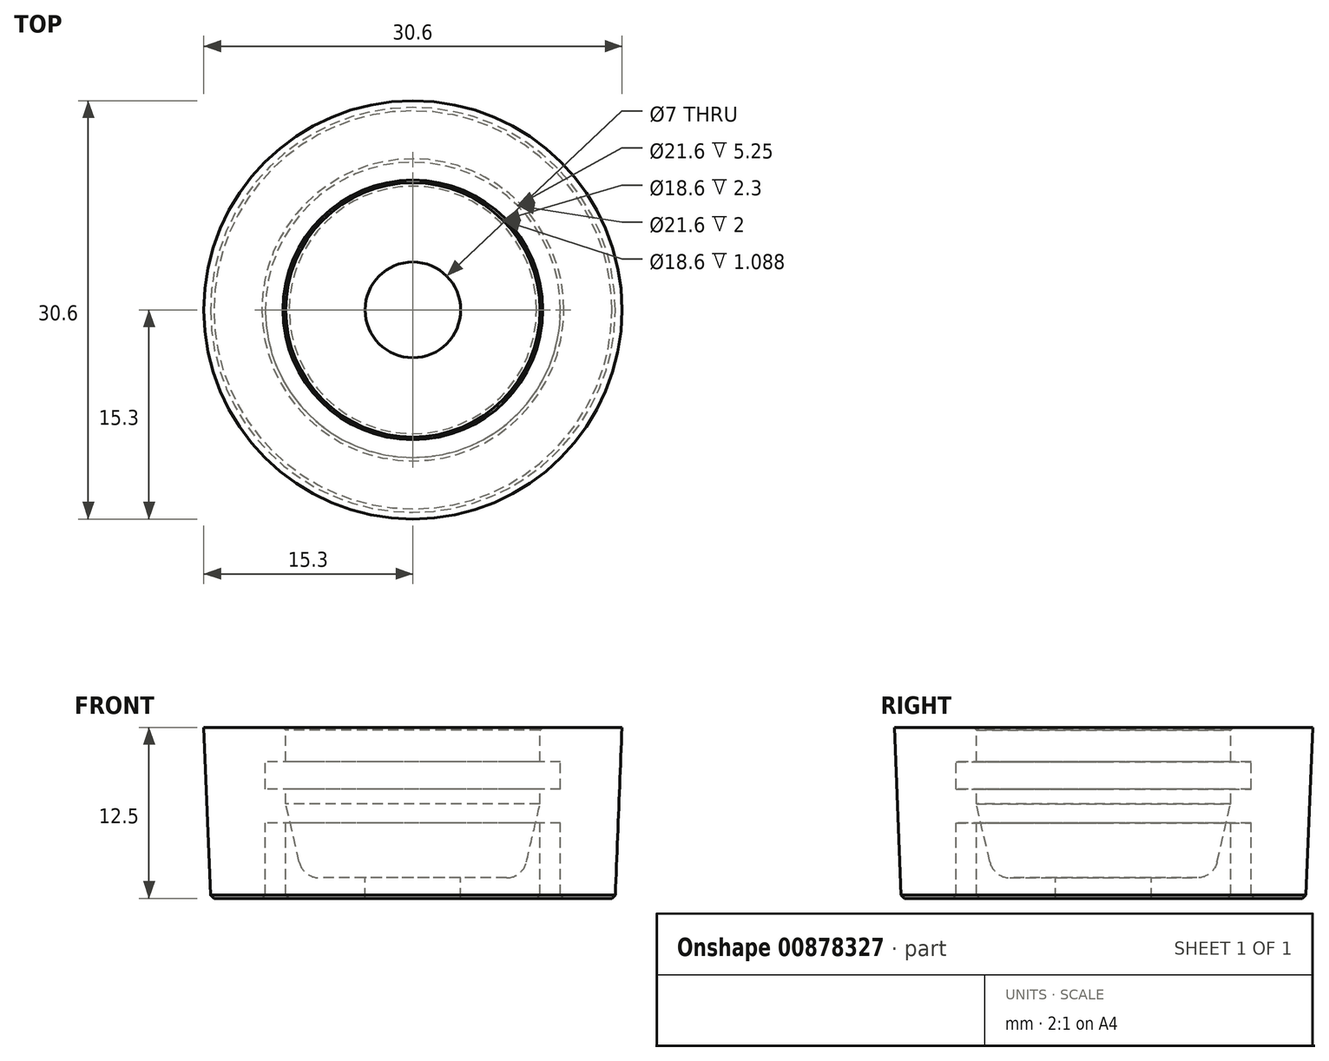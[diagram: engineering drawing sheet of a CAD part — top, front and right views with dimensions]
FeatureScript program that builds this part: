
annotation { "Feature Type Name" : "Feature", "Feature Type Description" : "" }
export const myFeature = defineFeature(function(context is Context, id is Id, definition is map)
    precondition{}
    {
        {
            var Q0;
            Q0=qCreatedBy(makeId("Front.planeOp"),FACE);
            var sketch = newSketch(context, id + "F0", { "sketchPlane" : qUnion([Q0])});
            skLineSegment(sketch, "E0", {"start": v(3.5, -4) * mm, "end": v(8.04, -4) * mm});
            skLineSegment(sketch, "E1", {"start": v(8.04, -4) * mm, "end": v(9.3, 1.41) * mm});
            skLineSegment(sketch, "E2", {"start": v(9.3, 1.41) * mm, "end": v(9.3, 1.41) * mm});
            skLineSegment(sketch, "E3", {"start": v(9.3, 1.41) * mm, "end": v(9.3, 2.5) * mm});
            skLineSegment(sketch, "E4", {"start": v(9.3, 2.5) * mm, "end": v(10.8, 2.5) * mm});
            skLineSegment(sketch, "E5", {"start": v(10.8, 2.5) * mm, "end": v(10.8, 4.5) * mm});
            skLineSegment(sketch, "E6", {"start": v(10.8, 4.5) * mm, "end": v(9.3, 4.5) * mm});
            skLineSegment(sketch, "E7", {"start": v(9.3, 4.5) * mm, "end": v(9.3, 7) * mm});
            skLineSegment(sketch, "E8", {"start": v(9.3, 7) * mm, "end": v(15.3, 7) * mm});
            skLineSegment(sketch, "E9", {"start": v(15.3, 7) * mm, "end": v(14.8, -5.5) * mm});
            skLineSegment(sketch, "E10", {"start": v(14.8, -5.5) * mm, "end": v(10.8, -5.5) * mm});
            skLineSegment(sketch, "E11", {"start": v(10.8, -5.5) * mm, "end": v(10.8, 0) * mm});
            skLineSegment(sketch, "E12", {"start": v(10.8, 0) * mm, "end": v(9.3, 0) * mm});
            skLineSegment(sketch, "E13", {"start": v(9.3, 0) * mm, "end": v(9.3, -5.5) * mm});
            skLineSegment(sketch, "E14", {"start": v(9.3, -5.5) * mm, "end": v(3.5, -5.5) * mm});
            skLineSegment(sketch, "E15", {"start": v(3.5, -5.5) * mm, "end": v(3.5, -4) * mm});
            skLineSegment(sketch, "E16", {"start": v(0, 37.2) * mm, "end": v(0, -24.44) * mm, "construction": true});
            skSolve(sketch);
        }
        {
            var Q0;
            Q0 = qSketchRegion(id + "F0", true);
            var Q1;
            Q1=sQuery(id+"F0.wireOp",EDGE,"E16");
            revolve(context, id + "F1", {"surfaceOperationType" : NewSurfaceOperationType.NEW, "entities" : qUnion([Q0]), "axis" : qUnion([Q1]), "revolveType" : RevolveType.FULL});
        }
        {
            var Q0;
            Q0=makeQuery(id+"F1.opRevolve","SWEPT_EDGE",EDGE,{"disambiguationData":[OSD([sQuery(id+"F0.wireOp",EDGE,"E7"),sQuery(id+"F0.wireOp",EDGE,"E8")])]});
            chamfer(context, id + "F2", {"entities" : qUnion([Q0]), "width" : .2 * mm, "tangentPropagation" : true});
        }
        {
            var Q0;
            Q0=makeQuery(id+"F1.opRevolve","SWEPT_EDGE",EDGE,{"disambiguationData":[OSD([sQuery(id+"F0.wireOp",EDGE,"E0"),sQuery(id+"F0.wireOp",EDGE,"E1")])]});
            fillet(context, id + "F3", {"entities" : qUnion([Q0]), "radius" : 1.5 * mm, "tangentPropagation" : true, "allowEdgeOverflow" : false});
        }
        {
            var Q0;
            Q0=makeQuery(id+"F1.opRevolve","SWEPT_EDGE",EDGE,{"disambiguationData":[OSD([sQuery(id+"F0.wireOp",EDGE,"E9"),sQuery(id+"F0.wireOp",EDGE,"E10")])]});
            var Q1;
            Q1=makeQuery(id+"F1.opRevolve","SWEPT_EDGE",EDGE,{"disambiguationData":[OSD([sQuery(id+"F0.wireOp",EDGE,"E10"),sQuery(id+"F0.wireOp",EDGE,"E11")])]});
            var Q2;
            Q2=makeQuery(id+"F1.opRevolve","SWEPT_EDGE",EDGE,{"disambiguationData":[OSD([sQuery(id+"F0.wireOp",EDGE,"E13"),sQuery(id+"F0.wireOp",EDGE,"E14")])]});
            chamfer(context, id + "F4", {"entities" : qUnion([Q0, Q1, Q2]), "width" : .25 * mm, "tangentPropagation" : true});
        }
    });
